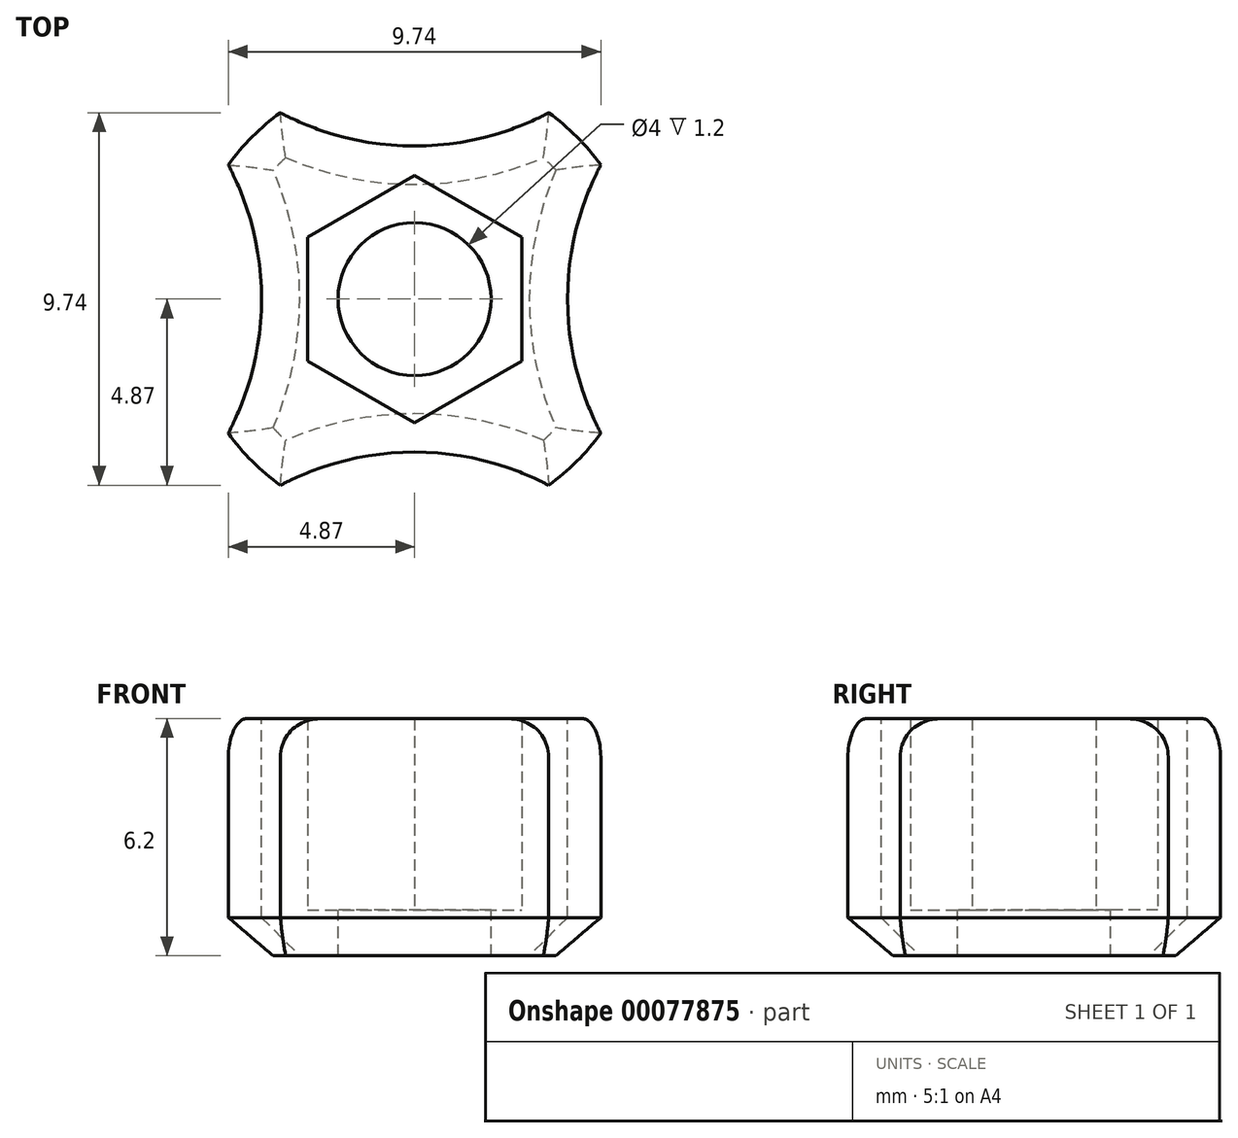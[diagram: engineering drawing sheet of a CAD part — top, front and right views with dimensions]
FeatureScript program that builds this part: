
annotation { "Feature Type Name" : "Feature", "Feature Type Description" : "" }
export const myFeature = defineFeature(function(context is Context, id is Id, definition is map)
    precondition{}
    {
        {
            var Q0;
            Q0=qCreatedBy(makeId("Top.planeOp"),FACE);
            var sketch = newSketch(context, id + "F0", { "sketchPlane" : qUnion([Q0])});
            skCircle(sketch, "E0", {"center": v(0, 0) * mm, "radius": 6 * mm});
            skCircle(sketch, "E1", {"center": v(0, 0) * mm, "radius": 2 * mm});
            skCircle(sketch, "E2.cCircle", {"center": v(0, 0) * mm, "radius": 2.8 * mm, "construction": true});
            skLineSegment(sketch, "E2.0", {"start": v(2.8, 1.62) * mm, "end": v(2.8, -1.62) * mm});
            skLineSegment(sketch, "E2.1", {"start": v(2.8, -1.62) * mm, "end": v(0, -3.23) * mm});
            skLineSegment(sketch, "E2.2", {"start": v(0, -3.23) * mm, "end": v(-2.8, -1.62) * mm});
            skLineSegment(sketch, "E2.3", {"start": v(-2.8, -1.62) * mm, "end": v(-2.8, 1.62) * mm});
            skLineSegment(sketch, "E2.4", {"start": v(-2.8, 1.62) * mm, "end": v(0, 3.23) * mm});
            skLineSegment(sketch, "E2.5", {"start": v(0, 3.23) * mm, "end": v(2.8, 1.62) * mm});
            skPoint(sketch, "E2.0.midPoint", {"position": v(2.8, 0) * mm});
            skSolve(sketch);
        }
        {
            var Q0;
            Q0=makeQuery(id+"F0.imprint","IMPRINT",FACE,{"disambiguationData":[TD([[makeQuery(id+"F0.imprint","IMPRINT",EDGE,{"derivedFrom":sQuery(id+"F0.wireOp",EDGE,"E0")}),1.0]])]});
            var Q1;
            Q1=makeQuery(id+"F0.imprint","IMPRINT",FACE,{"disambiguationData":[TD([[makeQuery(id+"F0.imprint","IMPRINT",EDGE,{"derivedFrom":sQuery(id+"F0.wireOp",EDGE,"E1")}),-1.0]])]});
            extrude(context, id + "F1", {"entities" : qUnion([Q0, Q1]), "oppositeDirection" : true, "depth" : 1.2 * mm});
        }
        {
            var Q0;
            Q0=makeQuery(id+"F0.imprint","IMPRINT",FACE,{"disambiguationData":[TD([[makeQuery(id+"F0.imprint","IMPRINT",EDGE,{"derivedFrom":sQuery(id+"F0.wireOp",EDGE,"E0")}),1.0]])]});
            extrude(context, id + "F2", {"entities" : qUnion([Q0]), "operationType" : NewBodyOperationType.ADD, "depth" : 5 * mm});
        }
        {
            var Q0;
            Q0=makeQuery(id+"F2.opExtrude","CAP_FACE",FACE,{"disambiguationData":[OSD([sQuery(id+"F0.wireOp",EDGE,"E0"),sQuery(id+"F0.wireOp",EDGE,"E2.0"),sQuery(id+"F0.wireOp",EDGE,"E2.1"),sQuery(id+"F0.wireOp",EDGE,"E2.2"),sQuery(id+"F0.wireOp",EDGE,"E2.3"),sQuery(id+"F0.wireOp",EDGE,"E2.4"),sQuery(id+"F0.wireOp",EDGE,"E2.5")])],"isStart":false});
            var sketch = newSketch(context, id + "F3", { "sketchPlane" : qUnion([Q0])});
            skCircle(sketch, "E3", {"center": v(-11.5, 0) * mm, "radius": 7.5 * mm});
            skSolve(sketch);
        }
        {
            var Q0;
            {var subQ0=sQuery(id+"F3.wireOp",EDGE,"E3");var subQ1=makeQuery(id+"F2.opExtrude","CAP_EDGE",EDGE,{"disambiguationData":[OSD([sQuery(id+"F0.wireOp",EDGE,"E0")])],"isStart":false});var subQ2=makeQuery(id+"F3.imprint","INTERSECT",VERTEX,{"disambiguationData":[OD(0.0)],"derivedFrom":[subQ1,subQ0]});Q0=makeQuery(id+"F3.imprint","IMPRINT",FACE,{"disambiguationData":[TD([[makeQuery(id+"F3.imprint","IMPRINT",EDGE,{"disambiguationData":[TD([[subQ2,-1.0]])],"derivedFrom":subQ0}),1.0]])]});}
            extrude(context, id + "F4", {"entities" : qUnion([Q0]), "oppositeDirection" : true, "depth" : 25 * mm});
        }
        {
            var Q0;
            Q0=makeQuery(id+"F4.opExtrude","SWEPT_BODY",BODY,{"disambiguationData":[OSD([sQuery(id+"F0.wireOp",EDGE,"E0"),sQuery(id+"F3.wireOp",EDGE,"E3")])]});
            var Q1;
            {var subQ0=sQuery(id+"F0.wireOp",EDGE,"E0");Q1=makeQuery(id+"F2.boolean.opBoolean","MERGE",FACE,{"derivedFrom":[makeQuery(id+"F1.opExtrude","SWEPT_FACE",FACE,{"disambiguationData":[OSD([subQ0])]}),makeQuery(id+"F2.opExtrude","SWEPT_FACE",FACE,{"disambiguationData":[OSD([subQ0])]})]});}
            circularPattern(context, id + "F5", {"operationType" : NewBodyOperationType.REMOVE, "entities" : qUnion([Q0]), "axis" : qUnion([Q1]), "angle" : 90 * degree, "instanceCount" : 4});
        }
        {
            var Q0;
            Q0=makeQuery(id+"F5.boolean.opBoolean","COPY",EDGE,{"derivedFrom":makeQuery(id+"F5.opPattern","COPY",EDGE,{"derivedFrom":makeQuery(id+"F4.opExtrude","CAP_EDGE",EDGE,{"disambiguationData":[OSD([sQuery(id+"F3.wireOp",EDGE,"E3")])],"isStart":true}),"instanceName":"1"})});
            var Q1;
            {var subQ0=sQuery(id+"F0.wireOp",EDGE,"E0");var subQ1=makeQuery(id+"F4.opExtrude","SWEPT_FACE",FACE,{"disambiguationData":[OSD([sQuery(id+"F3.wireOp",EDGE,"E3")])]});Q1=makeQuery(id+"F5.boolean.opBoolean","SPLIT",EDGE,{"disambiguationData":[TD([makeQuery(id+"F1.opExtrude","SWEPT_FACE",FACE,{"disambiguationData":[OSD([subQ0])]}),makeQuery(id+"F2.opExtrude","SWEPT_FACE",FACE,{"disambiguationData":[OSD([subQ0])]}),makeQuery(id+"F2.opExtrude","CAP_FACE",FACE,{"disambiguationData":[OSD([subQ0,sQuery(id+"F0.wireOp",EDGE,"E2.0"),sQuery(id+"F0.wireOp",EDGE,"E2.1"),sQuery(id+"F0.wireOp",EDGE,"E2.2"),sQuery(id+"F0.wireOp",EDGE,"E2.3"),sQuery(id+"F0.wireOp",EDGE,"E2.4"),sQuery(id+"F0.wireOp",EDGE,"E2.5")])],"isStart":false}),subQ1,makeQuery(id+"F5.opPattern","COPY",FACE,{"derivedFrom":subQ1,"instanceName":"1"})])],"derivedFrom":makeQuery(id+"F2.opExtrude","CAP_EDGE",EDGE,{"disambiguationData":[OSD([subQ0])],"isStart":false})});}
            var Q2;
            Q2=makeQuery(id+"F5.boolean.opBoolean","COPY",EDGE,{"derivedFrom":makeQuery(id+"F4.opExtrude","CAP_EDGE",EDGE,{"disambiguationData":[OSD([sQuery(id+"F3.wireOp",EDGE,"E3")])],"isStart":true})});
            var Q3;
            {var subQ0=sQuery(id+"F0.wireOp",EDGE,"E0");var subQ1=makeQuery(id+"F4.opExtrude","SWEPT_FACE",FACE,{"disambiguationData":[OSD([sQuery(id+"F3.wireOp",EDGE,"E3")])]});Q3=makeQuery(id+"F5.boolean.opBoolean","SPLIT",EDGE,{"disambiguationData":[TD([makeQuery(id+"F1.opExtrude","SWEPT_FACE",FACE,{"disambiguationData":[OSD([subQ0])]}),makeQuery(id+"F2.opExtrude","SWEPT_FACE",FACE,{"disambiguationData":[OSD([subQ0])]}),makeQuery(id+"F2.opExtrude","CAP_FACE",FACE,{"disambiguationData":[OSD([subQ0,sQuery(id+"F0.wireOp",EDGE,"E2.0"),sQuery(id+"F0.wireOp",EDGE,"E2.1"),sQuery(id+"F0.wireOp",EDGE,"E2.2"),sQuery(id+"F0.wireOp",EDGE,"E2.3"),sQuery(id+"F0.wireOp",EDGE,"E2.4"),sQuery(id+"F0.wireOp",EDGE,"E2.5")])],"isStart":false}),subQ1,makeQuery(id+"F5.opPattern","COPY",FACE,{"derivedFrom":subQ1,"instanceName":"3"})])],"derivedFrom":makeQuery(id+"F2.opExtrude","CAP_EDGE",EDGE,{"disambiguationData":[OSD([subQ0])],"isStart":false})});}
            var Q4;
            Q4=makeQuery(id+"F5.boolean.opBoolean","COPY",EDGE,{"derivedFrom":makeQuery(id+"F5.opPattern","COPY",EDGE,{"derivedFrom":makeQuery(id+"F4.opExtrude","CAP_EDGE",EDGE,{"disambiguationData":[OSD([sQuery(id+"F3.wireOp",EDGE,"E3")])],"isStart":true}),"instanceName":"3"})});
            var Q5;
            {var subQ0=makeQuery(id+"F4.opExtrude","SWEPT_FACE",FACE,{"disambiguationData":[OSD([sQuery(id+"F3.wireOp",EDGE,"E3")])]});var subQ1=sQuery(id+"F0.wireOp",EDGE,"E0");Q5=makeQuery(id+"F5.boolean.opBoolean","SPLIT",EDGE,{"disambiguationData":[TD([makeQuery(id+"F1.opExtrude","SWEPT_FACE",FACE,{"disambiguationData":[OSD([subQ1])]}),makeQuery(id+"F2.opExtrude","SWEPT_FACE",FACE,{"disambiguationData":[OSD([subQ1])]}),makeQuery(id+"F2.opExtrude","CAP_FACE",FACE,{"disambiguationData":[OSD([subQ1,sQuery(id+"F0.wireOp",EDGE,"E2.0"),sQuery(id+"F0.wireOp",EDGE,"E2.1"),sQuery(id+"F0.wireOp",EDGE,"E2.2"),sQuery(id+"F0.wireOp",EDGE,"E2.3"),sQuery(id+"F0.wireOp",EDGE,"E2.4"),sQuery(id+"F0.wireOp",EDGE,"E2.5")])],"isStart":false}),makeQuery(id+"F5.opPattern","COPY",FACE,{"derivedFrom":subQ0,"instanceName":"2"}),makeQuery(id+"F5.opPattern","COPY",FACE,{"derivedFrom":subQ0,"instanceName":"3"})])],"derivedFrom":makeQuery(id+"F2.opExtrude","CAP_EDGE",EDGE,{"disambiguationData":[OSD([subQ1])],"isStart":false})});}
            var Q6;
            Q6=makeQuery(id+"F5.boolean.opBoolean","COPY",EDGE,{"derivedFrom":makeQuery(id+"F5.opPattern","COPY",EDGE,{"derivedFrom":makeQuery(id+"F4.opExtrude","CAP_EDGE",EDGE,{"disambiguationData":[OSD([sQuery(id+"F3.wireOp",EDGE,"E3")])],"isStart":true}),"instanceName":"2"})});
            var Q7;
            {var subQ0=makeQuery(id+"F4.opExtrude","SWEPT_FACE",FACE,{"disambiguationData":[OSD([sQuery(id+"F3.wireOp",EDGE,"E3")])]});var subQ1=sQuery(id+"F0.wireOp",EDGE,"E0");Q7=makeQuery(id+"F5.boolean.opBoolean","SPLIT",EDGE,{"disambiguationData":[TD([makeQuery(id+"F1.opExtrude","SWEPT_FACE",FACE,{"disambiguationData":[OSD([subQ1])]}),makeQuery(id+"F2.opExtrude","SWEPT_FACE",FACE,{"disambiguationData":[OSD([subQ1])]}),makeQuery(id+"F2.opExtrude","CAP_FACE",FACE,{"disambiguationData":[OSD([subQ1,sQuery(id+"F0.wireOp",EDGE,"E2.0"),sQuery(id+"F0.wireOp",EDGE,"E2.1"),sQuery(id+"F0.wireOp",EDGE,"E2.2"),sQuery(id+"F0.wireOp",EDGE,"E2.3"),sQuery(id+"F0.wireOp",EDGE,"E2.4"),sQuery(id+"F0.wireOp",EDGE,"E2.5")])],"isStart":false}),makeQuery(id+"F5.opPattern","COPY",FACE,{"derivedFrom":subQ0,"instanceName":"1"}),makeQuery(id+"F5.opPattern","COPY",FACE,{"derivedFrom":subQ0,"instanceName":"2"})])],"derivedFrom":makeQuery(id+"F2.opExtrude","CAP_EDGE",EDGE,{"disambiguationData":[OSD([subQ1])],"isStart":false})});}
            fillet(context, id + "F6", {"entities" : qUnion([Q0, Q1, Q2, Q3, Q4, Q5, Q6, Q7]), "radius" : 1 * mm, "tangentPropagation" : true, "allowEdgeOverflow" : false});
        }
        {
            var Q0;
            {var subQ0=sQuery(id+"F0.wireOp",EDGE,"E0");var subQ1=makeQuery(id+"F4.opExtrude","SWEPT_FACE",FACE,{"disambiguationData":[OSD([sQuery(id+"F3.wireOp",EDGE,"E3")])]});Q0=makeQuery(id+"F5.boolean.opBoolean","SPLIT",EDGE,{"disambiguationData":[TD([makeQuery(id+"F1.opExtrude","SWEPT_FACE",FACE,{"disambiguationData":[OSD([subQ0])]}),makeQuery(id+"F1.opExtrude","CAP_FACE",FACE,{"disambiguationData":[OSD([subQ0,sQuery(id+"F0.wireOp",EDGE,"E1")])],"isStart":false}),makeQuery(id+"F2.opExtrude","SWEPT_FACE",FACE,{"disambiguationData":[OSD([subQ0])]}),subQ1,makeQuery(id+"F5.opPattern","COPY",FACE,{"derivedFrom":subQ1,"instanceName":"1"})])],"derivedFrom":makeQuery(id+"F1.opExtrude","CAP_EDGE",EDGE,{"disambiguationData":[OSD([subQ0])],"isStart":false})});}
            var Q1;
            Q1=makeQuery(id+"F5.boolean.opBoolean","INTERSECT",EDGE,{"derivedFrom":[makeQuery(id+"F1.opExtrude","CAP_FACE",FACE,{"disambiguationData":[OSD([sQuery(id+"F0.wireOp",EDGE,"E0"),sQuery(id+"F0.wireOp",EDGE,"E1")])],"isStart":false}),makeQuery(id+"F5.opPattern","COPY",FACE,{"derivedFrom":makeQuery(id+"F4.opExtrude","SWEPT_FACE",FACE,{"disambiguationData":[OSD([sQuery(id+"F3.wireOp",EDGE,"E3")])]}),"instanceName":"1"})]});
            var Q2;
            {var subQ0=makeQuery(id+"F4.opExtrude","SWEPT_FACE",FACE,{"disambiguationData":[OSD([sQuery(id+"F3.wireOp",EDGE,"E3")])]});var subQ1=sQuery(id+"F0.wireOp",EDGE,"E0");Q2=makeQuery(id+"F5.boolean.opBoolean","SPLIT",EDGE,{"disambiguationData":[TD([makeQuery(id+"F1.opExtrude","SWEPT_FACE",FACE,{"disambiguationData":[OSD([subQ1])]}),makeQuery(id+"F1.opExtrude","CAP_FACE",FACE,{"disambiguationData":[OSD([subQ1,sQuery(id+"F0.wireOp",EDGE,"E1")])],"isStart":false}),makeQuery(id+"F2.opExtrude","SWEPT_FACE",FACE,{"disambiguationData":[OSD([subQ1])]}),makeQuery(id+"F5.opPattern","COPY",FACE,{"derivedFrom":subQ0,"instanceName":"1"}),makeQuery(id+"F5.opPattern","COPY",FACE,{"derivedFrom":subQ0,"instanceName":"2"})])],"derivedFrom":makeQuery(id+"F1.opExtrude","CAP_EDGE",EDGE,{"disambiguationData":[OSD([subQ1])],"isStart":false})});}
            var Q3;
            Q3=makeQuery(id+"F5.boolean.opBoolean","INTERSECT",EDGE,{"derivedFrom":[makeQuery(id+"F1.opExtrude","CAP_FACE",FACE,{"disambiguationData":[OSD([sQuery(id+"F0.wireOp",EDGE,"E0"),sQuery(id+"F0.wireOp",EDGE,"E1")])],"isStart":false}),makeQuery(id+"F5.opPattern","COPY",FACE,{"derivedFrom":makeQuery(id+"F4.opExtrude","SWEPT_FACE",FACE,{"disambiguationData":[OSD([sQuery(id+"F3.wireOp",EDGE,"E3")])]}),"instanceName":"2"})]});
            var Q4;
            Q4=makeQuery(id+"F5.boolean.opBoolean","INTERSECT",EDGE,{"derivedFrom":[makeQuery(id+"F1.opExtrude","CAP_FACE",FACE,{"disambiguationData":[OSD([sQuery(id+"F0.wireOp",EDGE,"E0"),sQuery(id+"F0.wireOp",EDGE,"E1")])],"isStart":false}),makeQuery(id+"F5.opPattern","COPY",FACE,{"derivedFrom":makeQuery(id+"F4.opExtrude","SWEPT_FACE",FACE,{"disambiguationData":[OSD([sQuery(id+"F3.wireOp",EDGE,"E3")])]}),"instanceName":"3"})]});
            var Q5;
            {var subQ0=sQuery(id+"F0.wireOp",EDGE,"E0");var subQ1=makeQuery(id+"F4.opExtrude","SWEPT_FACE",FACE,{"disambiguationData":[OSD([sQuery(id+"F3.wireOp",EDGE,"E3")])]});Q5=makeQuery(id+"F5.boolean.opBoolean","SPLIT",EDGE,{"disambiguationData":[TD([makeQuery(id+"F1.opExtrude","SWEPT_FACE",FACE,{"disambiguationData":[OSD([subQ0])]}),makeQuery(id+"F1.opExtrude","CAP_FACE",FACE,{"disambiguationData":[OSD([subQ0,sQuery(id+"F0.wireOp",EDGE,"E1")])],"isStart":false}),makeQuery(id+"F2.opExtrude","SWEPT_FACE",FACE,{"disambiguationData":[OSD([subQ0])]}),subQ1,makeQuery(id+"F5.opPattern","COPY",FACE,{"derivedFrom":subQ1,"instanceName":"3"})])],"derivedFrom":makeQuery(id+"F1.opExtrude","CAP_EDGE",EDGE,{"disambiguationData":[OSD([subQ0])],"isStart":false})});}
            var Q6;
            {var subQ0=makeQuery(id+"F4.opExtrude","SWEPT_FACE",FACE,{"disambiguationData":[OSD([sQuery(id+"F3.wireOp",EDGE,"E3")])]});var subQ1=sQuery(id+"F0.wireOp",EDGE,"E0");Q6=makeQuery(id+"F5.boolean.opBoolean","SPLIT",EDGE,{"disambiguationData":[TD([makeQuery(id+"F1.opExtrude","SWEPT_FACE",FACE,{"disambiguationData":[OSD([subQ1])]}),makeQuery(id+"F1.opExtrude","CAP_FACE",FACE,{"disambiguationData":[OSD([subQ1,sQuery(id+"F0.wireOp",EDGE,"E1")])],"isStart":false}),makeQuery(id+"F2.opExtrude","SWEPT_FACE",FACE,{"disambiguationData":[OSD([subQ1])]}),makeQuery(id+"F5.opPattern","COPY",FACE,{"derivedFrom":subQ0,"instanceName":"2"}),makeQuery(id+"F5.opPattern","COPY",FACE,{"derivedFrom":subQ0,"instanceName":"3"})])],"derivedFrom":makeQuery(id+"F1.opExtrude","CAP_EDGE",EDGE,{"disambiguationData":[OSD([subQ1])],"isStart":false})});}
            var Q7;
            Q7=makeQuery(id+"F5.boolean.opBoolean","INTERSECT",EDGE,{"derivedFrom":[makeQuery(id+"F1.opExtrude","CAP_FACE",FACE,{"disambiguationData":[OSD([sQuery(id+"F0.wireOp",EDGE,"E0"),sQuery(id+"F0.wireOp",EDGE,"E1")])],"isStart":false}),makeQuery(id+"F4.opExtrude","SWEPT_FACE",FACE,{"disambiguationData":[OSD([sQuery(id+"F3.wireOp",EDGE,"E3")])]})]});
            chamfer(context, id + "F7", {"entities" : qUnion([Q0, Q1, Q2, Q3, Q4, Q5, Q6, Q7]), "width" : 1 * mm, "tangentPropagation" : true});
        }
    });
